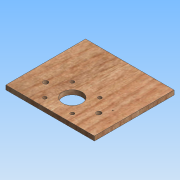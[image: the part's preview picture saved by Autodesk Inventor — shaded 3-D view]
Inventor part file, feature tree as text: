
AUTODESK INVENTOR PART (.ipt)
format: ipt  version: 2015 (Build 190159000, 159)  size: 341,504 bytes
history: native  units: mm
features: sketch x15, other x9, extrude x9, hole x3, projected_geometry x1
ambient origin geometry x8: Origin, YZ Plane, XZ Plane, XY Plane, X Axis, Y Axis, Z Axis, Center Point
bodies: Body1 (feature_tree)
feature tree (37):
  other  "Blocks"
  extrude  "Extrusion2"  Depth=50.0mm
  hole  "Hole4"  [1 undecoded]
  hole  "Hole5"  [1 undecoded]
  hole  "Hole8"  [1 undecoded]
  extrude  "Extrusion5"  Depth=20.0mm
  extrude  "Extrusion6"  TaperAngle=0.0deg  [1 undecoded]
  extrude  "Extrusion10"  Depth=10.0mm
  extrude  "Extrusion11"  Depth=5.5mm
  extrude  "Extrusion12"  Depth=40.0mm
  extrude  "Extrusion13"  Depth=5.0mm
  extrude  "Extrusion15"  Depth=5.0mm TaperAngle=0.0deg
  extrude  "Extrusion16"  Depth=5.0mm
  sketch  "Sketch42"  dims[d129=5.5mm d130=0.0mm]
  sketch  "Sketch43"  dims[d131=5.5mm d132=10.0mm]
  sketch  "Sketch41"  dims[d122=5.5mm d123=20.0mm]
  sketch  "Sketch10"  dims[d21=100.0mm d22=50.0mm]
  sketch  "Sketch13"  dims[d23=5.0mm d24=0.0mm d43=31.0mm]
  sketch  "Sketch16"  dims[d44=31.0mm]
  sketch  "Sketch17"  dims[d45=4.0mm d46=6.0mm d47=4.0mm d48=2.0mm d49=90.0deg d50=4.0mm d51=0.0mm d52=60.0mm]
  sketch  "Sketch33"  dims[d53=5.2mm d54=6.0mm d55=4.0mm d56=2.0mm d57=90.0deg d58=4.0mm d59=0.0mm]
  sketch  "Sketch34"  dims[d78=22.0mm d79=6.0mm d80=4.0mm d81=2.0mm d82=90.0deg d83=2.0mm d84=0.0mm d121=20.0mm]
  other  "Block1"
  other  "Block2"
  other  "Block3"
  other  "Block4"
  sketch  "Sketch45"  dims[d133=8.333333mm d134=5.5mm]
  projected_geometry  "Projected Loop4"
  sketch  "Sketch46"  dims[d135=0.0mm d189=40.0mm]
  sketch  "Sketch47"  dims[d190=5.0mm d191=0.0mm d192=5.0mm]
  sketch  "Sketch48"  dims[d193=5.0mm d194=5.0mm d195=0.0mm]
  sketch  "Sketch50"  dims[d196=5.0mm d197=5.0mm]
  sketch  "Sketch51"  dims[d198=5.0mm d199=0.0mm d200=20.0mm d201=5.0mm d202=5.0mm d203=20.0mm d204=5.0mm d205=0.0mm d210=5.0mm d211=5.0mm d212=20.0mm d213=5.0mm d214=5.0mm d215=20.0mm d216=5.0mm d217=0.0mm d218=5.0mm d219=5.0mm d220=40.0mm d221=5.0mm d222=5.0mm d223=40.0mm d224=5.0mm d225=0.0mm d29=1.0mm d30=1.0mm]
  other  "Block3:1"
  other  "Block3:2"
  other  "Block4:1"
  other  "Block4:2"
note: 4 required parameter values undecoded (feature->parameter linkage not recoverable at this tier; creation-order binding heuristic only, values carry confidence <= 0.55)
